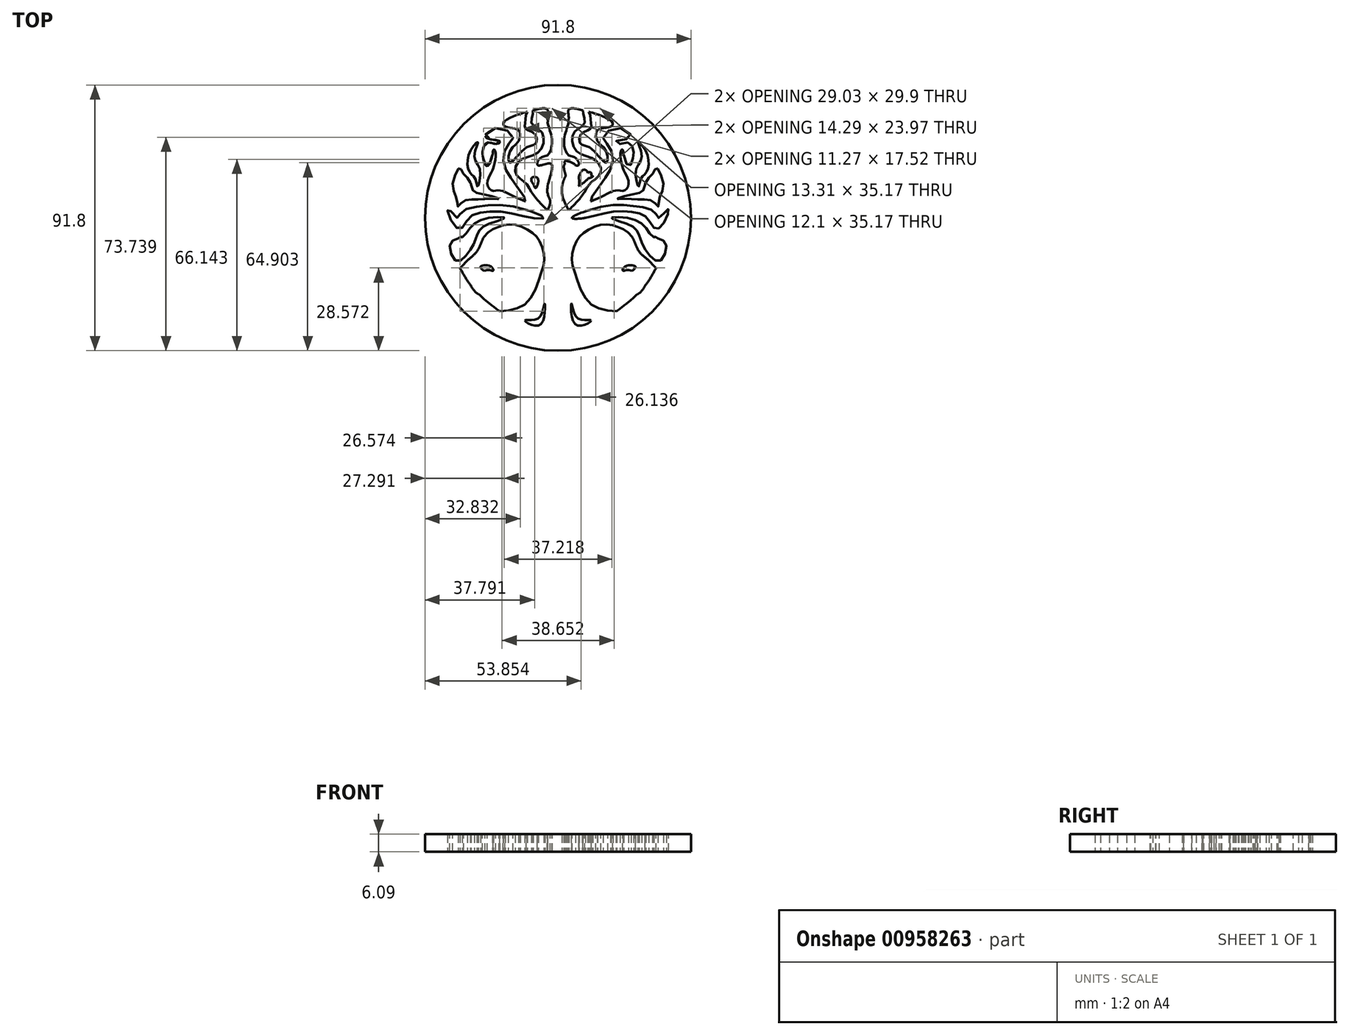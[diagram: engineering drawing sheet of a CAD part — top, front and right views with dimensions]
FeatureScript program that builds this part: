
annotation { "Feature Type Name" : "Feature", "Feature Type Description" : "" }
export const myFeature = defineFeature(function(context is Context, id is Id, definition is map)
    precondition{}
    {
        {
            var Q0;
            Q0=qCreatedBy(makeId("Top.planeOp"),FACE);
            var sketch = newSketch(context, id + "F0", { "sketchPlane" : qUnion([Q0])});
            skLineSegment(sketch, "E0", {"start": v(0, 12.7) * mm, "end": v(0, -12.7) * mm, "construction": true});
            skFitSpline(sketch, "E1", {"points": [v(-11.28, -5.78) * mm, v(-9.32, -3.87) * mm, v(-8.52, -2.2) * mm, v(-7.35, -1.25) * mm, v(-5.99, -0.81) * mm, v(-4.38, -0.94) * mm, v(-2.84, -1.81) * mm, v(-2.08, -2.77) * mm, v(-1.58, -4.62) * mm, v(-1.96, -6.39) * mm, v(-3.6, -9.8) * mm, v(-6.74, -10.76) * mm], "startDerivative": vector(19.24, 20) * mm, "endDerivative": vector(-30.15, -2.58) * mm});
            skFitSpline(sketch, "E2", {"points": [v(-11.28, -5.78) * mm, v(-9.77, -8.12) * mm, v(-6.74, -10.76) * mm], "startDerivative": vector(2.95, -5.31) * mm, "endDerivative": vector(6.15, -4.78) * mm});
            skFitSpline(sketch, "E3", {"points": [v(-11.69, -4.97) * mm, v(-10.22, -3.88) * mm, v(-9.52, -2.53) * mm, v(-9.1, -1.5) * mm, v(-7.9, -0.67) * mm, v(-6.12, 0) * mm, v(-7.9, 0) * mm, v(-9.99, -1) * mm, v(-11.03, -2.23) * mm, v(-12.37, -2.88) * mm, v(-11.69, -4.97) * mm]});
            skFitSpline(sketch, "E4", {"points": [v(-3.14, 0) * mm, v(-6.12, 0.68) * mm, v(-8.82, 0.63) * mm, v(-10.24, 0) * mm, v(-11.15, -1.23) * mm, v(-12.14, -0.63) * mm, v(-12.66, 1.01) * mm, v(-11.58, 0) * mm, v(-11.15, 0.63) * mm, v(-8.92, 1.33) * mm, v(-5.28, 1.33) * mm, v(-1.6, 0) * mm, v(-3.14, 0) * mm]});
            skFitSpline(sketch, "E5", {"points": [v(-9.25, -3.81) * mm, v(-9.43, -5.26) * mm, v(-9.9, -6.68) * mm, v(-10, -7.6) * mm, v(-9.62, -8.07) * mm, v(-9.22, -7.59) * mm, v(-9.39, -6.98) * mm, v(-9.04, -6.07) * mm, v(-8.66, -4.88) * mm, v(-8.55, -3.42) * mm, v(-8.52, -2.18) * mm, v(-8.48, -2.11) * mm], "startDerivative": vector(-0.87, -12.47) * mm, "endDerivative": vector(1.86, 1.52) * mm});
            skFitSpline(sketch, "E6", {"points": [v(-11.28, -5.78) * mm, v(-10.6, -5.07) * mm, v(-9.32, -3.87) * mm], "startDerivative": vector(2.34, 1.68) * mm, "endDerivative": vector(1.64, 2.16) * mm});
            skFitSpline(sketch, "E7", {"points": [v(-12.12, 3.8) * mm, v(-11.65, 2.16) * mm, v(-11.53, 1.3) * mm, v(-10.93, 1.9) * mm, v(-9.46, 2.09) * mm, v(-7.72, 2.2) * mm, v(-6.77, 2.16) * mm, v(-8.47, 2.7) * mm, v(-9.76, 3.1) * mm, v(-10.21, 4.32) * mm, v(-11, 5.22) * mm, v(-11.32, 5.76) * mm, v(-12.12, 3.8) * mm]});
            skFitSpline(sketch, "E8", {"points": [v(-10.05, 7.77) * mm, v(-10.4, 5.94) * mm, v(-10.02, 5.07) * mm, v(-9.5, 4.47) * mm, v(-9.27, 3.6) * mm, v(-8.96, 5.45) * mm, v(-9.64, 7.07) * mm, v(-9.23, 8.72) * mm, v(-10.05, 7.77) * mm]});
            skFitSpline(sketch, "E9", {"points": [v(-8.36, 9.28) * mm, v(-6.69, 8.82) * mm, v(-6.99, 8.52) * mm, v(-8.12, 8.67) * mm, v(-8.58, 8.13) * mm, v(-8.69, 7.35) * mm, v(-8.54, 6.6) * mm, v(-8.2, 5.95) * mm, v(-7.67, 6.79) * mm, v(-7.4, 7.88) * mm, v(-7.18, 7.54) * mm, v(-7.37, 6) * mm, v(-7.7, 5.2) * mm, v(-8.13, 3.94) * mm, v(-7.62, 3.15) * mm, v(-6.84, 3.16) * mm, v(-5.48, 2.7) * mm, v(-3.7, 1.91) * mm, v(-4.69, 3.58) * mm, v(-5.8, 5.16) * mm, v(-6.31, 6.79) * mm, v(-5.74, 8.45) * mm, v(-5.17, 9.24) * mm, v(-6.97, 10.37) * mm, v(-8.36, 9.28) * mm]});
            skFitSpline(sketch, "E10", {"points": [v(-9.32, -3.87) * mm, v(-9.25, -3.81) * mm], "startDerivative": vector(0.07, 0.06) * mm, "endDerivative": vector(0.07, 0.06) * mm});
            skFitSpline(sketch, "E11", {"points": [v(0, 0) * mm, v(-2.87, 2.71) * mm, v(-3.77, 4.04) * mm, v(-4.9, 5.18) * mm, v(-4.3, 6.65) * mm, v(-2.15, 7.67) * mm, v(-1.85, 9.82) * mm, v(-3.06, 10.95) * mm, v(-2.88, 12.37) * mm, v(-3.54, 12.2) * mm, v(-3.77, 11.03) * mm, v(-3.77, 10.31) * mm, v(-2.68, 9.67) * mm, v(-2.57, 8.54) * mm, v(-3.66, 8.09) * mm, v(-5.57, 6.35) * mm, v(-5.5, 7.73) * mm, v(-4.54, 8.84) * mm, v(-4.57, 10.11) * mm, v(-6.03, 10.49) * mm, v(-6.15, 11.12) * mm, v(-3.6, 12.18) * mm, v(-3.74, 12.13) * mm, v(-3.85, 12.1) * mm], "startDerivative": vector(-50.4, 31.67) * mm, "endDerivative": vector(-2.98, -0.99) * mm});
            skFitSpline(sketch, "E12", {"points": [v(-3.6, 12.18) * mm, v(-3.54, 12.2) * mm], "startDerivative": vector(0.11, 0.03) * mm, "endDerivative": vector(0.11, 0.03) * mm});
            skFitSpline(sketch, "E13", {"points": [v(-1.24, 0.78) * mm, v(-0.9, 1.88) * mm, v(-1.24, 3.27) * mm, v(-0.8, 6.22) * mm, v(-2.33, 6.05) * mm, v(-2.02, 6.9) * mm, v(-1.24, 7.2) * mm, v(-0.69, 8.96) * mm, v(-1.24, 11.31) * mm, v(-1.24, 12.48) * mm, v(-2.88, 12.37) * mm], "startDerivative": vector(4.03, 10.4) * mm, "endDerivative": vector(-20.33, -6.55) * mm});
            skFitSpline(sketch, "E14.MirrorCS", {"points": [v(9.32, -3.87) * mm, v(9.25, -3.81) * mm], "startDerivative": vector(-0.07, 0.06) * mm, "endDerivative": vector(-0.07, 0.06) * mm});
            skFitSpline(sketch, "E15.MirrorCS", {"points": [v(3.6, 12.18) * mm, v(3.54, 12.2) * mm], "startDerivative": vector(-0.11, 0.03) * mm, "endDerivative": vector(-0.11, 0.03) * mm});
            skFitSpline(sketch, "E16.trimOffspring", {"points": [v(0, 0) * mm, v(-2.87, 2.71) * mm, v(-3.77, 4.04) * mm, v(-4.9, 5.18) * mm, v(-4.3, 6.65) * mm, v(-2.15, 7.67) * mm, v(-1.85, 9.82) * mm, v(-3.06, 10.95) * mm, v(-2.88, 12.37) * mm, v(-3.54, 12.2) * mm, v(-3.77, 11.03) * mm, v(-3.77, 10.31) * mm, v(-2.68, 9.67) * mm, v(-2.57, 8.54) * mm, v(-3.66, 8.09) * mm, v(-5.57, 6.35) * mm, v(-5.5, 7.73) * mm, v(-4.54, 8.84) * mm, v(-4.57, 10.11) * mm, v(-6.03, 10.49) * mm, v(-6.15, 11.12) * mm, v(-3.6, 12.18) * mm, v(-3.74, 12.13) * mm, v(-3.85, 12.1) * mm], "startDerivative": vector(-50.4, 31.67) * mm, "endDerivative": vector(-2.98, -0.99) * mm});
            skFitSpline(sketch, "E17", {"points": [v(-11.49, -2.4) * mm, v(-11.65, -2.98) * mm, v(-11.3, -3.46) * mm, v(-11.16, -3.78) * mm, v(-10.82, -3.17) * mm, v(-10.6, -2.81) * mm, v(-11.03, -2.23) * mm, v(-11.49, -2.4) * mm]});
            skFitSpline(sketch, "E18", {"points": [v(-10.02, 3.81) * mm, v(-10.12, 3.43) * mm, v(-10.57, 3.26) * mm, v(-11.17, 3.22) * mm, v(-10.93, 3.74) * mm, v(-10.54, 4.06) * mm, v(-10.1, 4.06) * mm, v(-10.02, 3.81) * mm]});
            skFitSpline(sketch, "E19", {"points": [v(-6.34, 3.09) * mm, v(-6.46, 3.51) * mm, v(-5.98, 4.39) * mm, v(-5.83, 3.48) * mm, v(-6.04, 2.98) * mm, v(-6.34, 3.09) * mm]});
            skFitSpline(sketch, "E20", {"points": [v(-8.89, -5.72) * mm, v(-8.55, -6.07) * mm, v(-7.95, -6) * mm, v(-7.45, -6.07) * mm, v(-7.73, -5.6) * mm, v(-8.82, -5.53) * mm, v(-8.89, -5.72) * mm]});
            skFitSpline(sketch, "E21", {"points": [v(-9.22, -7.59) * mm, v(-9.14, -8.77) * mm, v(-10, -7.83) * mm, v(-10, -7.1) * mm], "startDerivative": vector(1.1, -4.88) * mm, "endDerivative": vector(0.66, 2.28) * mm});
            skFitSpline(sketch, "E22", {"points": [v(-3.81, -11.83) * mm, v(-2.08, -12.32) * mm, v(-1.55, -9.86) * mm, v(-2.23, -11.52) * mm, v(-3.81, -11.83) * mm]});
            skFitSpline(sketch, "E23", {"points": [v(-7.51, 7.6) * mm, v(-7.77, 7.76) * mm, v(-8.36, 7.5) * mm, v(-8.27, 7.49) * mm, v(-8.06, 7.32) * mm, v(-7.57, 7.26) * mm, v(-7.51, 7.6) * mm]});
            skFitSpline(sketch, "E24", {"points": [v(-4.36, 9.4) * mm, v(-4.36, 9.2) * mm, v(-4.15, 9.3) * mm, v(-3.6, 8.64) * mm, v(-4.15, 8.75) * mm, v(-4.49, 8.92) * mm, v(-4.54, 8.84) * mm, v(-4.78, 8.54) * mm], "startDerivative": vector(-0.35, -2.81) * mm, "endDerivative": vector(-1.94, -2.21) * mm});
            skFitSpline(sketch, "E25", {"points": [v(-1.24, 11.43) * mm, v(-1.6, 11.74) * mm, v(-2.65, 11.6) * mm, v(-2.05, 11.14) * mm, v(-1.47, 10.81) * mm, v(-1.2, 10.98) * mm, v(-1.24, 11.43) * mm]});
            skFitSpline(sketch, "E26.MirrorCS", {"points": [v(9.22, -7.59) * mm, v(9.14, -8.77) * mm, v(10, -7.83) * mm, v(10, -7.1) * mm], "startDerivative": vector(-1.1, -4.88) * mm, "endDerivative": vector(-0.66, 2.28) * mm});
            skFitSpline(sketch, "E27.MirrorCS", {"points": [v(9.25, -3.81) * mm, v(9.43, -5.26) * mm, v(9.9, -6.68) * mm, v(10, -7.6) * mm, v(9.62, -8.07) * mm, v(9.22, -7.59) * mm, v(9.39, -6.98) * mm, v(9.04, -6.07) * mm, v(8.66, -4.88) * mm, v(8.55, -3.42) * mm, v(8.52, -2.18) * mm, v(8.48, -2.11) * mm], "startDerivative": vector(0.87, -12.47) * mm, "endDerivative": vector(-1.86, 1.52) * mm});
            skFitSpline(sketch, "E28.MirrorCS", {"points": [v(7.51, 7.6) * mm, v(7.77, 7.76) * mm, v(8.36, 7.5) * mm, v(8.27, 7.49) * mm, v(8.06, 7.32) * mm, v(7.57, 7.26) * mm, v(7.51, 7.6) * mm]});
            skFitSpline(sketch, "E29.MirrorCS", {"points": [v(11.28, -5.78) * mm, v(9.77, -8.12) * mm, v(6.74, -10.76) * mm], "startDerivative": vector(-2.95, -5.31) * mm, "endDerivative": vector(-6.15, -4.78) * mm});
            skFitSpline(sketch, "E30.MirrorCS", {"points": [v(11.28, -5.78) * mm, v(10.6, -5.07) * mm, v(9.32, -3.87) * mm], "startDerivative": vector(-2.34, 1.68) * mm, "endDerivative": vector(-1.64, 2.16) * mm});
            skFitSpline(sketch, "E31.MirrorCS", {"points": [v(4.36, 9.4) * mm, v(4.36, 9.2) * mm, v(4.15, 9.3) * mm, v(3.6, 8.64) * mm, v(4.15, 8.75) * mm, v(4.49, 8.92) * mm, v(4.54, 8.84) * mm, v(4.78, 8.54) * mm], "startDerivative": vector(0.35, -2.81) * mm, "endDerivative": vector(1.94, -2.21) * mm});
            skFitSpline(sketch, "E32.MirrorCS", {"points": [v(6.34, 3.09) * mm, v(6.46, 3.51) * mm, v(5.98, 4.39) * mm, v(5.83, 3.48) * mm, v(6.04, 2.98) * mm, v(6.34, 3.09) * mm]});
            skFitSpline(sketch, "E33.MirrorCS", {"points": [v(11.49, -2.4) * mm, v(11.65, -2.98) * mm, v(11.3, -3.46) * mm, v(11.16, -3.78) * mm, v(10.82, -3.17) * mm, v(10.6, -2.81) * mm, v(11.03, -2.23) * mm, v(11.49, -2.4) * mm]});
            skFitSpline(sketch, "E34.MirrorCS", {"points": [v(10.02, 3.81) * mm, v(10.12, 3.43) * mm, v(10.57, 3.26) * mm, v(11.17, 3.22) * mm, v(10.93, 3.74) * mm, v(10.54, 4.06) * mm, v(10.1, 4.06) * mm, v(10.02, 3.81) * mm]});
            skFitSpline(sketch, "E35.MirrorCS", {"points": [v(0, 0) * mm, v(2.87, 2.71) * mm, v(3.77, 4.04) * mm, v(4.9, 5.18) * mm, v(4.3, 6.65) * mm, v(2.15, 7.67) * mm, v(1.85, 9.82) * mm, v(3.06, 10.95) * mm, v(2.88, 12.37) * mm, v(3.54, 12.2) * mm, v(3.77, 11.03) * mm, v(3.77, 10.31) * mm, v(2.68, 9.67) * mm, v(2.57, 8.54) * mm, v(3.66, 8.09) * mm, v(5.57, 6.35) * mm, v(5.5, 7.73) * mm, v(4.54, 8.84) * mm, v(4.57, 10.11) * mm, v(6.03, 10.49) * mm, v(6.15, 11.12) * mm, v(3.6, 12.18) * mm, v(3.74, 12.13) * mm, v(3.85, 12.1) * mm], "startDerivative": vector(50.4, 31.67) * mm, "endDerivative": vector(2.98, -0.99) * mm});
            skFitSpline(sketch, "E36.MirrorC", {"points": [v(3.14, 0) * mm, v(6.12, 0.68) * mm, v(8.82, 0.63) * mm, v(10.24, 0) * mm, v(11.15, -1.23) * mm, v(12.14, -0.63) * mm, v(12.66, 1.01) * mm, v(11.58, 0) * mm, v(11.15, 0.63) * mm, v(8.92, 1.33) * mm, v(5.28, 1.33) * mm, v(1.6, 0) * mm, v(3.14, 0) * mm]});
            skFitSpline(sketch, "E37.MirrorC", {"points": [v(3.81, -11.83) * mm, v(2.08, -12.32) * mm, v(1.55, -9.86) * mm, v(2.23, -11.52) * mm, v(3.81, -11.83) * mm]});
            skFitSpline(sketch, "E38.MirrorCS", {"points": [v(8.36, 9.28) * mm, v(6.69, 8.82) * mm, v(6.99, 8.52) * mm, v(8.12, 8.67) * mm, v(8.58, 8.13) * mm, v(8.69, 7.35) * mm, v(8.54, 6.6) * mm, v(8.2, 5.95) * mm, v(7.67, 6.79) * mm, v(7.4, 7.88) * mm, v(7.18, 7.54) * mm, v(7.37, 6) * mm, v(7.7, 5.2) * mm, v(8.13, 3.94) * mm, v(7.62, 3.15) * mm, v(6.84, 3.16) * mm, v(5.48, 2.7) * mm, v(3.7, 1.91) * mm, v(4.69, 3.58) * mm, v(5.8, 5.16) * mm, v(6.31, 6.79) * mm, v(5.74, 8.45) * mm, v(5.17, 9.24) * mm, v(6.97, 10.37) * mm, v(8.36, 9.28) * mm]});
            skFitSpline(sketch, "E39.MirrorCS", {"points": [v(11.69, -4.97) * mm, v(10.22, -3.88) * mm, v(9.52, -2.53) * mm, v(9.1, -1.5) * mm, v(7.9, -0.67) * mm, v(6.12, 0) * mm, v(7.9, 0) * mm, v(9.99, -1) * mm, v(11.03, -2.23) * mm, v(12.37, -2.88) * mm, v(11.69, -4.97) * mm]});
            skFitSpline(sketch, "E40.MirrorCS", {"points": [v(12.12, 3.8) * mm, v(11.65, 2.16) * mm, v(11.53, 1.3) * mm, v(10.93, 1.9) * mm, v(9.46, 2.09) * mm, v(7.72, 2.2) * mm, v(6.77, 2.16) * mm, v(8.47, 2.7) * mm, v(9.76, 3.1) * mm, v(10.21, 4.32) * mm, v(11, 5.22) * mm, v(11.32, 5.76) * mm, v(12.12, 3.8) * mm]});
            skFitSpline(sketch, "E41.MirrorCS", {"points": [v(11.28, -5.78) * mm, v(9.32, -3.87) * mm, v(8.52, -2.2) * mm, v(7.35, -1.25) * mm, v(5.99, -0.81) * mm, v(4.38, -0.94) * mm, v(2.84, -1.81) * mm, v(2.08, -2.77) * mm, v(1.58, -4.62) * mm, v(1.96, -6.39) * mm, v(3.6, -9.8) * mm, v(6.74, -10.76) * mm], "startDerivative": vector(-19.24, 20) * mm, "endDerivative": vector(30.15, -2.58) * mm});
            skFitSpline(sketch, "E42.MirrorCS", {"points": [v(0, 0) * mm, v(2.87, 2.71) * mm, v(3.77, 4.04) * mm, v(4.9, 5.18) * mm, v(4.3, 6.65) * mm, v(2.15, 7.67) * mm, v(1.85, 9.82) * mm, v(3.06, 10.95) * mm, v(2.88, 12.37) * mm, v(3.54, 12.2) * mm, v(3.77, 11.03) * mm, v(3.77, 10.31) * mm, v(2.68, 9.67) * mm, v(2.57, 8.54) * mm, v(3.66, 8.09) * mm, v(5.57, 6.35) * mm, v(5.5, 7.73) * mm, v(4.54, 8.84) * mm, v(4.57, 10.11) * mm, v(6.03, 10.49) * mm, v(6.15, 11.12) * mm, v(3.6, 12.18) * mm, v(3.74, 12.13) * mm, v(3.85, 12.1) * mm], "startDerivative": vector(50.4, 31.67) * mm, "endDerivative": vector(2.98, -0.99) * mm});
            skFitSpline(sketch, "E43.MirrorC", {"points": [v(10.05, 7.77) * mm, v(10.4, 5.94) * mm, v(10.02, 5.07) * mm, v(9.5, 4.47) * mm, v(9.27, 3.6) * mm, v(8.96, 5.45) * mm, v(9.64, 7.07) * mm, v(9.23, 8.72) * mm, v(10.05, 7.77) * mm]});
            skFitSpline(sketch, "E44.MirrorCS", {"points": [v(8.89, -5.72) * mm, v(8.55, -6.07) * mm, v(7.95, -6) * mm, v(7.45, -6.07) * mm, v(7.73, -5.6) * mm, v(8.82, -5.53) * mm, v(8.89, -5.72) * mm]});
            skFitSpline(sketch, "E45.MirrorCS", {"points": [v(1.24, 0.78) * mm, v(0.9, 1.88) * mm, v(1.24, 3.27) * mm, v(0.8, 6.22) * mm, v(2.33, 6.05) * mm, v(2.02, 6.9) * mm, v(1.24, 7.2) * mm, v(0.69, 8.96) * mm, v(1.24, 11.31) * mm, v(1.24, 12.48) * mm, v(2.88, 12.37) * mm], "startDerivative": vector(-4.03, 10.4) * mm, "endDerivative": vector(20.33, -6.55) * mm});
            skFitSpline(sketch, "E46.MirrorCS", {"points": [v(1.24, 11.43) * mm, v(1.6, 11.74) * mm, v(2.65, 11.6) * mm, v(2.05, 11.14) * mm, v(1.47, 10.81) * mm, v(1.2, 10.98) * mm, v(1.24, 11.43) * mm]});
            skFitSpline(sketch, "E47", {"points": [v(1.13, 1.08) * mm, v(0.53, 2.41) * mm, v(0.46, 3.59) * mm, v(0.81, 4.72) * mm, v(1.13, 5.68) * mm, v(0.8, 6.22) * mm, v(0.8, 6.52) * mm, v(1.63, 6.34) * mm, v(2.11, 5.7) * mm, v(1.8, 4.37) * mm, v(2.11, 3.76) * mm, v(2.45, 3.73) * mm, v(3.83, 5.08) * mm, v(3.58, 5.25) * mm, v(2.73, 4.58) * mm, v(2.45, 4.39) * mm, v(2.43, 4.87) * mm, v(2.94, 5.88) * mm, v(2.48, 6.7) * mm, v(2.02, 6.9) * mm], "startDerivative": vector(-10.22, 18.85) * mm, "endDerivative": vector(-10.76, 2.37) * mm});
            skFitSpline(sketch, "E48", {"points": [v(1.13, 1.08) * mm, v(1.2, 0.89) * mm], "startDerivative": vector(0.07, -0.2) * mm, "endDerivative": vector(0.07, -0.2) * mm});
            skFitSpline(sketch, "E49", {"points": [v(2.45, 4.39) * mm, v(2.45, 3.73) * mm], "startDerivative": vector(0, -0.65) * mm, "endDerivative": vector(0, -0.65) * mm});
            skFitSpline(sketch, "E50.trimOffspring", {"points": [v(1.13, 1.08) * mm, v(0.53, 2.41) * mm, v(0.46, 3.59) * mm, v(0.81, 4.72) * mm, v(1.13, 5.68) * mm, v(0.8, 6.22) * mm, v(0.8, 6.52) * mm, v(1.63, 6.34) * mm, v(2.11, 5.7) * mm, v(1.8, 4.37) * mm, v(2.11, 3.76) * mm, v(2.45, 3.73) * mm, v(3.83, 5.08) * mm, v(3.58, 5.25) * mm, v(2.73, 4.58) * mm, v(2.45, 4.39) * mm, v(2.43, 4.87) * mm, v(2.94, 5.88) * mm, v(2.48, 6.7) * mm, v(2.02, 6.9) * mm], "startDerivative": vector(-10.22, 18.85) * mm, "endDerivative": vector(-10.76, 2.37) * mm});
            skFitSpline(sketch, "E51", {"points": [v(2.4, 4.5) * mm, v(2.45, 4.04) * mm, v(2.37, 3.7) * mm, v(2.26, 3.68) * mm], "startDerivative": vector(0.22, -1.06) * mm, "endDerivative": vector(-0.56, 0.08) * mm});
            skFitSpline(sketch, "E52", {"points": [v(2.6, 5.2) * mm, v(2.74, 4.81) * mm, v(3.52, 4.56) * mm, v(4.01, 4.81) * mm, v(3.53, 5) * mm, v(3.32, 5.4) * mm, v(3.02, 5.54) * mm, v(2.78, 5.48) * mm], "startDerivative": vector(0.4, -3.04) * mm, "endDerivative": vector(-2.14, -0.87) * mm});
            skFitSpline(sketch, "E53", {"points": [v(-1.63, 6.15) * mm, v(-2.1, 5.9) * mm, v(-2.03, 5.37) * mm, v(-2.7, 4.63) * mm, v(-4.1, 5.95) * mm, v(-3.86, 6.14) * mm, v(-3.4, 5.54) * mm, v(-2.76, 5.2) * mm, v(-2.57, 5.82) * mm, v(-2.64, 6.33) * mm, v(-2.02, 6.9) * mm], "startDerivative": vector(-7.44, -2.35) * mm, "endDerivative": vector(7.83, 5.18) * mm});
            skFitSpline(sketch, "E54", {"points": [v(-2.92, 4.68) * mm, v(-3.08, 4.33) * mm, v(-2.76, 3.73) * mm, v(-2.58, 3.43) * mm, v(-2.28, 4.12) * mm, v(-2.33, 4.53) * mm, v(-2.48, 4.66) * mm, v(-2.92, 4.68) * mm]});
            skFitSpline(sketch, "E55", {"points": [v(-1.24, 3.27) * mm, v(-1.43, 2.17) * mm, v(-1.57, 1.81) * mm, v(-1.95, 1.9) * mm, v(-2.7, 2.47) * mm], "startDerivative": vector(-0.62, -3.73) * mm, "endDerivative": vector(-2.56, 2.26) * mm});
            skFitSpline(sketch, "E56", {"points": [v(0.46, 3.59) * mm, v(0.67, 2.63) * mm, v(1.25, 2.06) * mm, v(1.69, 2.04) * mm, v(2.1, 2.23) * mm, v(3.03, 2.95) * mm], "startDerivative": vector(0.38, -4.4) * mm, "endDerivative": vector(4.06, 3.36) * mm});
            skPoint(sketch, "E57.orphan", {"position": v(-1.2, 0.89) * mm});
            skFitSpline(sketch, "E58", {"points": [v(-3.94, 1) * mm, v(-3.5, 0.7) * mm, v(-3.47, 0.41) * mm, v(-4.28, 0.37) * mm, v(-5.35, 0.53) * mm], "startDerivative": vector(2.24, -1.1) * mm, "endDerivative": vector(-3.15, 0.52) * mm});
            skFitSpline(sketch, "E59", {"points": [v(3.37, 0.83) * mm, v(2.58, 0.32) * mm, v(2.62, 0) * mm, v(3.14, 0) * mm], "startDerivative": vector(-2.4, -1.02) * mm, "endDerivative": vector(1.96, 0.38) * mm});
            skSolve(sketch);
        }
        {
            var Q0;
            Q0=qCreatedBy(makeId("Top.planeOp"),FACE);
            var sketch = newSketch(context, id + "F1", { "sketchPlane" : qUnion([Q0])});
            skCircle(sketch, "E60", {"center": v(0, 0) * mm, "radius": 15.3 * mm});
            skSolve(sketch);
        }
        {
            var Q0;
            Q0 = qSketchRegion(id + "F1", true);
            extrude(context, id + "F2", {"entities" : qUnion([Q0]), "flatOperationType" : FlatOperationType.REMOVE, "depth" : 2.03 * mm, "offsetDistance" : 25.4 * mm, "domain" : OperationDomain.MODEL});
        }
        {
            var Q0;
            Q0 = qSketchRegion(id + "F0", true);
            extrude(context, id + "F3", {"entities" : qUnion([Q0]), "operationType" : NewBodyOperationType.REMOVE, "flatOperationType" : FlatOperationType.REMOVE, "depth" : 2.03 * mm, "offsetDistance" : 25.4 * mm, "domain" : OperationDomain.MODEL});
        }
        {
            var Q0;
            Q0=makeQuery(id+"F2.opExtrude","SWEPT_BODY",BODY,{"disambiguationData":[OSD([sQuery(id+"F1.wireOp",EDGE,"E60")])]});
            var Q1;
            Q1=qCreatedBy(makeId("Origin.pointOp"),VERTEX);
            transform(context, id + "F4", {"entities" : qUnion([Q0]), "transformType" : TransformType.SCALE_UNIFORMLY, "scale" : 3, "scalePoint" : qUnion([Q1]), "makeCopy" : false});
        }
    });
